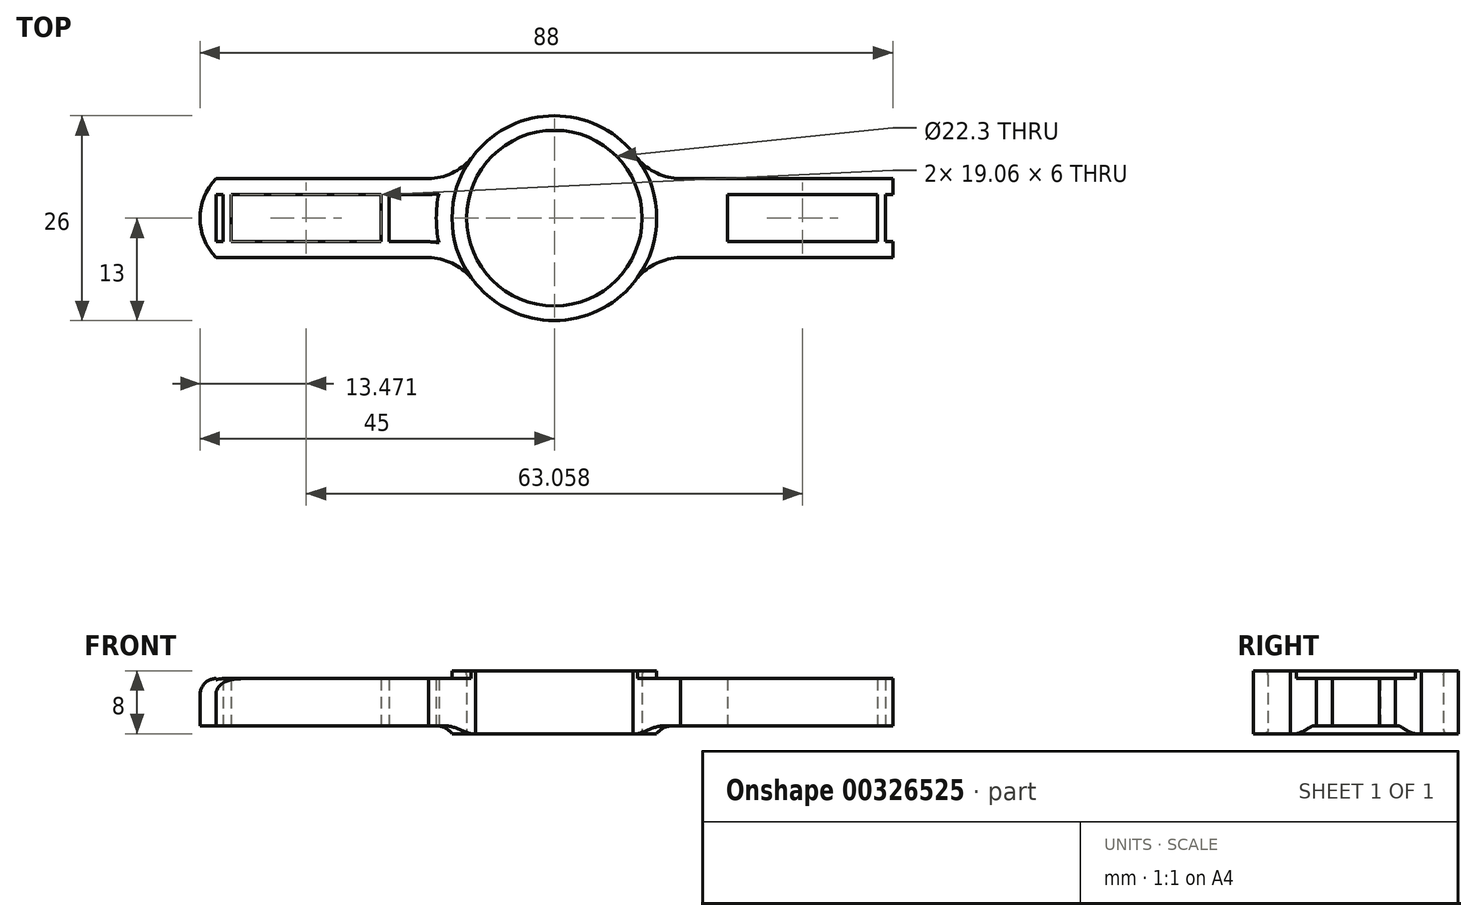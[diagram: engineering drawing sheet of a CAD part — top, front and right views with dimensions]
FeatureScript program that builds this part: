
annotation { "Feature Type Name" : "Feature", "Feature Type Description" : "" }
export const myFeature = defineFeature(function(context is Context, id is Id, definition is map)
    precondition{}
    {
        {
            var Q0;
            Q0=qCreatedBy(makeId("Top.planeOp"),FACE);
            var sketch = newSketch(context, id + "F0", { "sketchPlane" : qUnion([Q0])});
            skArc(sketch, "E0", {"start": v(0, 11.15) * mm, "mid": v(-11.15, 0) * mm, "end": v(0, -11.15) * mm});
            skArc(sketch, "E1", {"start": v(0, 13) * mm, "mid": v(-13, 0) * mm, "end": v(0, -13) * mm});
            skLineSegment(sketch, "E2.right", {"start": v(-45, 12) * mm, "end": v(-45, -15) * mm, "construction": true});
            skLineSegment(sketch, "E3", {"start": v(45, 15) * mm, "end": v(45, -15) * mm, "construction": true});
            skLineSegment(sketch, "E4", {"start": v(-10, 15) * mm, "end": v(45, 15) * mm, "construction": true});
            skLineSegment(sketch, "E5", {"start": v(45, -15) * mm, "end": v(-45, -15) * mm, "construction": true});
            skLineSegment(sketch, "E6.right", {"start": v(45, 0) * mm, "end": v(45, 5) * mm, "construction": true});
            skPoint(sketch, "E7.orphan", {"position": v(0, 39.35) * mm});
            skLineSegment(sketch, "E8.top", {"start": v(-16, 5) * mm, "end": v(-43, 5) * mm});
            skLineSegment(sketch, "E8.right", {"start": v(-43, 0) * mm, "end": v(-43, 5) * mm, "construction": true});
            skLineSegment(sketch, "E9.top", {"start": v(-16, -5) * mm, "end": v(-43, -5) * mm});
            skLineSegment(sketch, "E9.right", {"start": v(-43, 0) * mm, "end": v(-43, -5) * mm, "construction": true});
            skLineSegment(sketch, "E10", {"start": v(-43, 5) * mm, "end": v(-43, 12) * mm, "construction": true});
            skPoint(sketch, "E11", {"position": v(-45, 0) * mm});
            skArc(sketch, "E12", {"start": v(-43, 5) * mm, "mid": v(-45, 0) * mm, "end": v(-43, -5) * mm});
            skLineSegment(sketch, "E13.top", {"start": v(-45, 12) * mm, "end": v(-43, 12) * mm, "construction": true});
            skLineSegment(sketch, "E14.MirrorCS", {"start": v(-45, 12) * mm, "end": v(-10, 12) * mm, "construction": true});
            skLineSegment(sketch, "E15.MirrorCS", {"start": v(-45, -12) * mm, "end": v(-45, 15) * mm, "construction": true});
            skLineSegment(sketch, "E16.MirrorCS", {"start": v(-43, 5) * mm, "end": v(-43, 15) * mm, "construction": true});
            skLineSegment(sketch, "E17.MirrorCS", {"start": v(-10, 15) * mm, "end": v(-10, 12) * mm, "construction": true});
            skLineSegment(sketch, "E18.MirrorCS", {"start": v(45, 15) * mm, "end": v(-10, 15) * mm, "construction": true});
            skLineSegment(sketch, "E19", {"start": v(-41, 15) * mm, "end": v(-41, 5) * mm, "construction": true});
            skArc(sketch, "E20", {"start": v(-43, 12) * mm, "mid": v(-41.55, 13.2) * mm, "end": v(-41, 15) * mm});
            skLineSegment(sketch, "E21", {"start": v(-43, 5) * mm, "end": v(-43, 12) * mm});
            skLineSegment(sketch, "E22", {"start": v(-20, 15) * mm, "end": v(-20, -5) * mm, "construction": true});
            skLineSegment(sketch, "E23", {"start": v(-41, 15) * mm, "end": v(-20, 15) * mm});
            skArc(sketch, "E24", {"start": v(-10, 12) * mm, "mid": v(-14.78, 14.23) * mm, "end": v(-20, 15) * mm});
            skPoint(sketch, "E25", {"position": v(-20, 5) * mm});
            skPoint(sketch, "E26", {"position": v(-20, -5) * mm});
            skLineSegment(sketch, "E27", {"start": v(-45, 7) * mm, "end": v(-18, 7) * mm, "construction": true});
            skLineSegment(sketch, "E28", {"start": v(-18, 18.78) * mm, "end": v(-18, -5) * mm, "construction": true});
            skPoint(sketch, "E29", {"position": v(-18, 7) * mm});
            skPoint(sketch, "E30", {"position": v(-20, 0) * mm});
            skLineSegment(sketch, "E31", {"start": v(-20, 0) * mm, "end": v(-20, 5) * mm});
            skLineSegment(sketch, "E32", {"start": v(-18, 7) * mm, "end": v(-18, 7) * mm});
            skPoint(sketch, "E33.visualSharp", {"position": v(-20, 7) * mm});
            skArc(sketch, "E33.filletArc", {"start": v(-18, 7) * mm, "mid": v(-19.41, 6.41) * mm, "end": v(-20, 5) * mm});
            skArc(sketch, "E34", {"start": v(-18, 7) * mm, "mid": v(-13.28, 8.35) * mm, "end": v(-10, 12) * mm});
            skPoint(sketch, "E35.orphan", {"position": v(-10, -12) * mm});
            skPoint(sketch, "E36.MirrorCS.start.orphan", {"position": v(-10, -15) * mm});
            skPoint(sketch, "E37.MirrorCS.start.orphan", {"position": v(-45, -12) * mm});
            skPoint(sketch, "E38.end.orphan", {"position": v(-43, -15) * mm});
            skArc(sketch, "E39.MirrorCS", {"start": v(-10, -12) * mm, "mid": v(-14.78, -14.23) * mm, "end": v(-20, -15) * mm});
            skLineSegment(sketch, "E40.trimOffspring", {"start": v(-20, 15) * mm, "end": v(-45, 15) * mm, "construction": true});
            skLineSegment(sketch, "E41.MirrorCS", {"start": v(-20, -15) * mm, "end": v(-45, -15) * mm, "construction": true});
            skArc(sketch, "E42.MirrorCS", {"start": v(-43, -12) * mm, "mid": v(-41.55, -13.2) * mm, "end": v(-41, -15) * mm});
            skArc(sketch, "E43.MirrorCS", {"start": v(-18, -7) * mm, "mid": v(-13.28, -8.35) * mm, "end": v(-10, -12) * mm});
            skArc(sketch, "E44.MirrorCS", {"start": v(-18, -7) * mm, "mid": v(-19.41, -6.41) * mm, "end": v(-20, -5) * mm});
            skLineSegment(sketch, "E45.MirrorCS", {"start": v(-20, -15) * mm, "end": v(-20, 5) * mm, "construction": true});
            skLineSegment(sketch, "E46.MirrorCS", {"start": v(-43, -5) * mm, "end": v(-43, -15) * mm, "construction": true});
            skLineSegment(sketch, "E47", {"start": v(-43, -12) * mm, "end": v(-43, -5) * mm});
            skLineSegment(sketch, "E48", {"start": v(-20, -15) * mm, "end": v(-41, -15) * mm});
            skLineSegment(sketch, "E49", {"start": v(-10, 12) * mm, "end": v(-10, -19.96) * mm, "construction": true});
            skPoint(sketch, "E50", {"position": v(-10, 8.3) * mm});
            skPoint(sketch, "E51", {"position": v(-10, -8.3) * mm});
            skLineSegment(sketch, "E52", {"start": v(-16, 17.22) * mm, "end": v(-16, -19.7) * mm, "construction": true});
            skPoint(sketch, "E53", {"position": v(-16, 5) * mm});
            skPoint(sketch, "E54", {"position": v(-16, -5) * mm});
            skArc(sketch, "E55", {"start": v(-16, 5) * mm, "mid": v(-12.6, 5.93) * mm, "end": v(-10, 8.3) * mm});
            skArc(sketch, "E56.MirrorCS", {"start": v(-16, -5) * mm, "mid": v(-12.6, -5.93) * mm, "end": v(-10, -8.3) * mm});
            skArc(sketch, "E57.MirrorCS", {"start": v(43, 5) * mm, "mid": v(45, 0) * mm, "end": v(43, -5) * mm});
            skLineSegment(sketch, "E58.MirrorCS", {"start": v(43, 5) * mm, "end": v(43, 15) * mm, "construction": true});
            skLineSegment(sketch, "E59.MirrorCS", {"start": v(16, 5) * mm, "end": v(43, 5) * mm});
            skLineSegment(sketch, "E60.MirrorCS", {"start": v(16, -5) * mm, "end": v(43, -5) * mm});
            skArc(sketch, "E61.MirrorCS", {"start": v(16, 5) * mm, "mid": v(12.6, 5.93) * mm, "end": v(10, 8.3) * mm});
            skArc(sketch, "E62.MirrorCS", {"start": v(0, 13) * mm, "mid": v(13, 0) * mm, "end": v(0, -13) * mm});
            skArc(sketch, "E63.MirrorCS", {"start": v(0, 11.15) * mm, "mid": v(11.15, 0) * mm, "end": v(0, -11.15) * mm});
            skArc(sketch, "E64.MirrorCS", {"start": v(10, 12) * mm, "mid": v(14.78, 14.23) * mm, "end": v(20, 15) * mm});
            skArc(sketch, "E65.MirrorCS", {"start": v(18, 7) * mm, "mid": v(13.28, 8.35) * mm, "end": v(10, 12) * mm});
            skArc(sketch, "E66.MirrorCS", {"start": v(18, -7) * mm, "mid": v(13.28, -8.35) * mm, "end": v(10, -12) * mm});
            skArc(sketch, "E67.MirrorCS", {"start": v(10, -12) * mm, "mid": v(14.78, -14.23) * mm, "end": v(20, -15) * mm});
            skArc(sketch, "E68.MirrorCS", {"start": v(18, -7) * mm, "mid": v(19.41, -6.41) * mm, "end": v(20, -5) * mm});
            skArc(sketch, "E69.MirrorCS", {"start": v(18, 7) * mm, "mid": v(19.41, 6.41) * mm, "end": v(20, 5) * mm});
            skArc(sketch, "E70.MirrorCS", {"start": v(16, -5) * mm, "mid": v(12.6, -5.93) * mm, "end": v(10, -8.3) * mm});
            skArc(sketch, "E71.MirrorCS", {"start": v(43, -12) * mm, "mid": v(41.55, -13.2) * mm, "end": v(41, -15) * mm});
            skArc(sketch, "E72.MirrorCS", {"start": v(43, 12) * mm, "mid": v(41.55, 13.2) * mm, "end": v(41, 15) * mm});
            skLineSegment(sketch, "E73", {"start": v(43, 12) * mm, "end": v(43, 5) * mm});
            skLineSegment(sketch, "E74", {"start": v(43, -12) * mm, "end": v(43, -5) * mm});
            skLineSegment(sketch, "E75", {"start": v(20, -15) * mm, "end": v(41, -15) * mm});
            skLineSegment(sketch, "E76", {"start": v(41, 15) * mm, "end": v(20, 15) * mm});
            skLineSegment(sketch, "E77", {"start": v(43, -5) * mm, "end": v(43, 5) * mm});
            skLineSegment(sketch, "E78", {"start": v(20, -5) * mm, "end": v(20, 5) * mm});
            skSolve(sketch);
        }
        {
            var Q0;
            Q0=makeQuery(id+"F0.imprint","IMPRINT",FACE,{"disambiguationData":[TD([[makeQuery(id+"F0.imprint","IMPRINT",EDGE,{"derivedFrom":sQuery(id+"F0.wireOp",EDGE,"E0")}),-1.0]])]});
            extrude(context, id + "F1", {"entities" : qUnion([Q0]), "depth" : 8 * mm});
        }
        {
            var Q0;
            {var subQ0=sQuery(id+"F0.wireOp",EDGE,"E12");Q0=makeQuery(id+"F0.imprint","IMPRINT",FACE,{"disambiguationData":[TD([[makeQuery(id+"F0.imprint","IMPRINT",EDGE,{"derivedFrom":subQ0}),1.0]])]});}
            var Q1;
            {var subQ9=sQuery(id+"F0.wireOp",EDGE,"E78");Q1=makeQuery(id+"F0.imprint","IMPRINT",FACE,{"disambiguationData":[TD([[makeQuery(id+"F0.imprint","IMPRINT",EDGE,{"derivedFrom":subQ9}),1.0]])]});}
            var Q2;
            {var subQ0=sQuery(id+"F0.wireOp",EDGE,"E77");Q2=makeQuery(id+"F0.imprint","IMPRINT",FACE,{"disambiguationData":[TD([[makeQuery(id+"F0.imprint","IMPRINT",EDGE,{"derivedFrom":subQ0}),1.0]])]});}
            var Q3;
            Q3=makeQuery(id+"F0.imprint","IMPRINT",FACE,{"disambiguationData":[TD([[makeQuery(id+"F0.imprint","IMPRINT",EDGE,{"derivedFrom":sQuery(id+"F0.wireOp",EDGE,"E57.MirrorCS")}),-1.0]])]});
            extrude(context, id + "F2", {"entities" : qUnion([Q0, Q1, Q2, Q3]), "operationType" : NewBodyOperationType.ADD, "depth" : 7 * mm});
        }
        {
            var Q0;
            Q0=qCreatedBy(makeId("Top.planeOp"),FACE);
            var sketch = newSketch(context, id + "F3", { "sketchPlane" : qUnion([Q0])});
            skArc(sketch, "E79.0", {"start": v(14.67, 3.12) * mm, "mid": v(15, 0) * mm, "end": v(14.67, -3.12) * mm});
            skLineSegment(sketch, "E79.1", {"start": v(15.97, -3) * mm, "end": v(42.06, -3) * mm});
            skArc(sketch, "E79.3", {"start": v(14.67, -3.12) * mm, "mid": v(15.32, -3.04) * mm, "end": v(15.97, -3) * mm});
            skLineSegment(sketch, "E79.4", {"start": v(42.06, 3) * mm, "end": v(15.97, 3) * mm});
            skArc(sketch, "E79.5", {"start": v(15.97, 3) * mm, "mid": v(15.32, 3.04) * mm, "end": v(14.67, 3.12) * mm});
            skLineSegment(sketch, "E80.MirrorCS", {"start": v(-42.06, 3) * mm, "end": v(-15.97, 3) * mm});
            skLineSegment(sketch, "E81.MirrorCS", {"start": v(-15.97, -3) * mm, "end": v(-42.06, -3) * mm});
            skArc(sketch, "E82.MirrorCS", {"start": v(-15.97, 3) * mm, "mid": v(-15.32, 3.04) * mm, "end": v(-14.67, 3.12) * mm});
            skArc(sketch, "E83.MirrorCS", {"start": v(-14.67, 3.12) * mm, "mid": v(-15, 0) * mm, "end": v(-14.67, -3.12) * mm});
            skArc(sketch, "E84.MirrorCS", {"start": v(-14.67, -3.12) * mm, "mid": v(-15.32, -3.04) * mm, "end": v(-15.97, -3) * mm});
            skLineSegment(sketch, "E85", {"start": v(-21, 17.8) * mm, "end": v(-21, -20.14) * mm, "construction": true});
            skLineSegment(sketch, "E86", {"start": v(-43, 17.17) * mm, "end": v(-43, -19.3) * mm, "construction": true});
            skPoint(sketch, "E87", {"position": v(-21, 3) * mm});
            skPoint(sketch, "E88", {"position": v(-21, -3) * mm});
            skPoint(sketch, "E89", {"position": v(-43, 3) * mm});
            skPoint(sketch, "E90", {"position": v(-43, -3) * mm});
            skLineSegment(sketch, "E91.bottom", {"start": v(-21, 3) * mm, "end": v(-22, 3) * mm});
            skLineSegment(sketch, "E91.top", {"start": v(-21, -3) * mm, "end": v(-22, -3) * mm});
            skLineSegment(sketch, "E91.left", {"start": v(-21, 3) * mm, "end": v(-21, -3) * mm});
            skLineSegment(sketch, "E91.right", {"start": v(-22, 3) * mm, "end": v(-22, -3) * mm});
            skLineSegment(sketch, "E92", {"start": v(-42.06, 3) * mm, "end": v(-43, 3) * mm});
            skLineSegment(sketch, "E93", {"start": v(-42.06, -3) * mm, "end": v(-43, -3) * mm});
            skLineSegment(sketch, "E94", {"start": v(-42.06, 3) * mm, "end": v(-42.06, -3) * mm});
            skLineSegment(sketch, "E95", {"start": v(-43, -3) * mm, "end": v(-43, 3) * mm});
            skLineSegment(sketch, "E96.bottom", {"start": v(-42.06, -3) * mm, "end": v(-41.06, -3) * mm});
            skLineSegment(sketch, "E96.top", {"start": v(-42.06, 3) * mm, "end": v(-41.06, 3) * mm});
            skLineSegment(sketch, "E96.left", {"start": v(-42.06, -3) * mm, "end": v(-42.06, 3) * mm});
            skLineSegment(sketch, "E96.right", {"start": v(-41.06, -3) * mm, "end": v(-41.06, 3) * mm});
            skLineSegment(sketch, "E97.bottom", {"start": v(-22, -3) * mm, "end": v(-23, -3) * mm});
            skLineSegment(sketch, "E97.top", {"start": v(-22, 3) * mm, "end": v(-23, 3) * mm});
            skLineSegment(sketch, "E97.left", {"start": v(-22, -3) * mm, "end": v(-22, 3) * mm});
            skLineSegment(sketch, "E98.MirrorCS", {"start": v(22, -3) * mm, "end": v(22, 3) * mm});
            skLineSegment(sketch, "E99.MirrorCS", {"start": v(41.06, -3) * mm, "end": v(41.06, 3) * mm});
            skLineSegment(sketch, "E100.MirrorCS", {"start": v(42.06, -3) * mm, "end": v(42.06, 3) * mm});
            skLineSegment(sketch, "E101.MirrorCS", {"start": v(43, 17.17) * mm, "end": v(43, -19.3) * mm, "construction": true});
            skPoint(sketch, "E102.MirrorP", {"position": v(43, 3) * mm});
            skLineSegment(sketch, "E103.MirrorCS", {"start": v(42.06, 3) * mm, "end": v(43, 3) * mm});
            skLineSegment(sketch, "E104.MirrorCS", {"start": v(42.06, -3) * mm, "end": v(43, -3) * mm});
            skLineSegment(sketch, "E105.MirrorCS", {"start": v(21, 17.8) * mm, "end": v(21, -20.14) * mm, "construction": true});
            skPoint(sketch, "E106", {"position": v(21, 3) * mm});
            skPoint(sketch, "E107", {"position": v(21, -3) * mm});
            skLineSegment(sketch, "E108", {"start": v(43, 3) * mm, "end": v(43, -3) * mm});
            skLineSegment(sketch, "E109", {"start": v(21, 3) * mm, "end": v(21, -3) * mm});
            skSolve(sketch);
        }
        {
            var Q0;
            {var subQ0=sQuery(id+"F3.wireOp",EDGE,"E96.right");Q0=makeQuery(id+"F3.imprint","IMPRINT",FACE,{"disambiguationData":[TD([[makeQuery(id+"F3.imprint","IMPRINT",EDGE,{"derivedFrom":subQ0}),-1.0]])]});}
            var Q1;
            Q1=makeQuery(id+"F3.imprint","IMPRINT",FACE,{"disambiguationData":[TD([[makeQuery(id+"F3.imprint","IMPRINT",EDGE,{"derivedFrom":sQuery(id+"F3.wireOp",EDGE,"E92")}),1.0]])]});
            var Q2;
            {var subQ0=sQuery(id+"F3.wireOp",EDGE,"E82.MirrorCS");Q2=makeQuery(id+"F3.imprint","IMPRINT",FACE,{"disambiguationData":[TD([[makeQuery(id+"F3.imprint","IMPRINT",EDGE,{"derivedFrom":subQ0}),-1.0]])]});}
            var Q3;
            Q3=makeQuery(id+"F3.imprint","IMPRINT",FACE,{"disambiguationData":[TD([[makeQuery(id+"F3.imprint","IMPRINT",EDGE,{"derivedFrom":sQuery(id+"F3.wireOp",EDGE,"E79.0")}),1.0]])]});
            var Q4;
            {var subQ0=sQuery(id+"F3.wireOp",EDGE,"E98.MirrorCS");Q4=makeQuery(id+"F3.imprint","IMPRINT",FACE,{"disambiguationData":[TD([[makeQuery(id+"F3.imprint","IMPRINT",EDGE,{"derivedFrom":subQ0}),-1.0]])]});}
            var Q5;
            Q5=makeQuery(id+"F3.imprint","IMPRINT",FACE,{"disambiguationData":[TD([[makeQuery(id+"F3.imprint","IMPRINT",EDGE,{"derivedFrom":sQuery(id+"F3.wireOp",EDGE,"E100.MirrorCS")}),-1.0]])]});
            extrude(context, id + "F4", {"entities" : qUnion([Q0, Q1, Q2, Q3, Q4, Q5]), "operationType" : NewBodyOperationType.REMOVE, "depth" : 7 * mm});
        }
        {
            var Q0;
            {var subQ0=sQuery(id+"F0.wireOp",EDGE,"E12");Q0=makeQuery(id+"F0.imprint","IMPRINT",FACE,{"disambiguationData":[TD([[makeQuery(id+"F0.imprint","IMPRINT",EDGE,{"derivedFrom":subQ0}),1.0]])]});}
            var Q1;
            {var subQ9=sQuery(id+"F0.wireOp",EDGE,"E78");Q1=makeQuery(id+"F0.imprint","IMPRINT",FACE,{"disambiguationData":[TD([[makeQuery(id+"F0.imprint","IMPRINT",EDGE,{"derivedFrom":subQ9}),1.0]])]});}
            var Q2;
            {var subQ0=sQuery(id+"F0.wireOp",EDGE,"E77");Q2=makeQuery(id+"F0.imprint","IMPRINT",FACE,{"disambiguationData":[TD([[makeQuery(id+"F0.imprint","IMPRINT",EDGE,{"derivedFrom":subQ0}),1.0]])]});}
            var Q3;
            Q3=makeQuery(id+"F0.imprint","IMPRINT",FACE,{"disambiguationData":[TD([[makeQuery(id+"F0.imprint","IMPRINT",EDGE,{"derivedFrom":sQuery(id+"F0.wireOp",EDGE,"E57.MirrorCS")}),-1.0]])]});
            extrude(context, id + "F5", {"entities" : qUnion([Q0, Q1, Q2, Q3]), "operationType" : NewBodyOperationType.REMOVE, "depth" : 1 * mm});
        }
        {
            var Q0;
            Q0=makeQuery(id+"F2.opExtrude","CAP_EDGE",EDGE,{"disambiguationData":[OSD([sQuery(id+"F0.wireOp",EDGE,"E1")])],"isStart":false});
            var Q1;
            Q1=makeQuery(id+"F2.opExtrude","CAP_EDGE",EDGE,{"disambiguationData":[OSD([sQuery(id+"F0.wireOp",EDGE,"E62.MirrorCS")])],"isStart":false});
            var Q2;
            Q2=makeQuery(id+"F5.boolean.opBoolean","COPY",EDGE,{"derivedFrom":makeQuery(id+"F5.opExtrude","CAP_EDGE",EDGE,{"disambiguationData":[OSD([sQuery(id+"F0.wireOp",EDGE,"E62.MirrorCS")])],"isStart":false})});
            var Q3;
            Q3=makeQuery(id+"F5.boolean.opBoolean","COPY",EDGE,{"derivedFrom":makeQuery(id+"F5.opExtrude","CAP_EDGE",EDGE,{"disambiguationData":[OSD([sQuery(id+"F0.wireOp",EDGE,"E1")])],"isStart":false})});
            fillet(context, id + "F6", {"entities" : qUnion([Q0, Q1, Q2, Q3]), "radius" : 2.5 * mm, "tangentPropagation" : true, "allowEdgeOverflow" : false});
        }
        {
            var Q0;
            Q0=makeQuery(id+"F2.opExtrude","CAP_EDGE",EDGE,{"disambiguationData":[OSD([sQuery(id+"F0.wireOp",EDGE,"E57.MirrorCS")])],"isStart":false});
            var Q1;
            Q1=makeQuery(id+"F5.boolean.opBoolean","COPY",EDGE,{"derivedFrom":makeQuery(id+"F5.opExtrude","CAP_EDGE",EDGE,{"disambiguationData":[OSD([sQuery(id+"F0.wireOp",EDGE,"E57.MirrorCS")])],"isStart":false})});
            var Q2;
            Q2=makeQuery(id+"F2.opExtrude","CAP_EDGE",EDGE,{"disambiguationData":[OSD([sQuery(id+"F0.wireOp",EDGE,"E12")])],"isStart":false});
            var Q3;
            Q3=makeQuery(id+"F5.boolean.opBoolean","COPY",EDGE,{"derivedFrom":makeQuery(id+"F5.opExtrude","CAP_EDGE",EDGE,{"disambiguationData":[OSD([sQuery(id+"F0.wireOp",EDGE,"E12")])],"isStart":false})});
            fillet(context, id + "F7", {"entities" : qUnion([Q0, Q1, Q2, Q3]), "radius" : 2 * mm, "tangentPropagation" : true, "allowEdgeOverflow" : false});
        }
        {
            var Q0;
            Q0=makeQuery(id+"F1.opExtrude","CAP_EDGE",EDGE,{"disambiguationData":[OSD([sQuery(id+"F0.wireOp",EDGE,"E0"),sQuery(id+"F0.wireOp",EDGE,"E63.MirrorCS")])],"isStart":true});
            var Q1;
            Q1=makeQuery(id+"F1.opExtrude","CAP_EDGE",EDGE,{"disambiguationData":[OSD([sQuery(id+"F0.wireOp",EDGE,"E0"),sQuery(id+"F0.wireOp",EDGE,"E63.MirrorCS")])],"isStart":false});
            fillet(context, id + "F8", {"entities" : qUnion([Q0, Q1]), "radius" : 0.5 * mm, "tangentPropagation" : true, "allowEdgeOverflow" : false});
        }
    });
